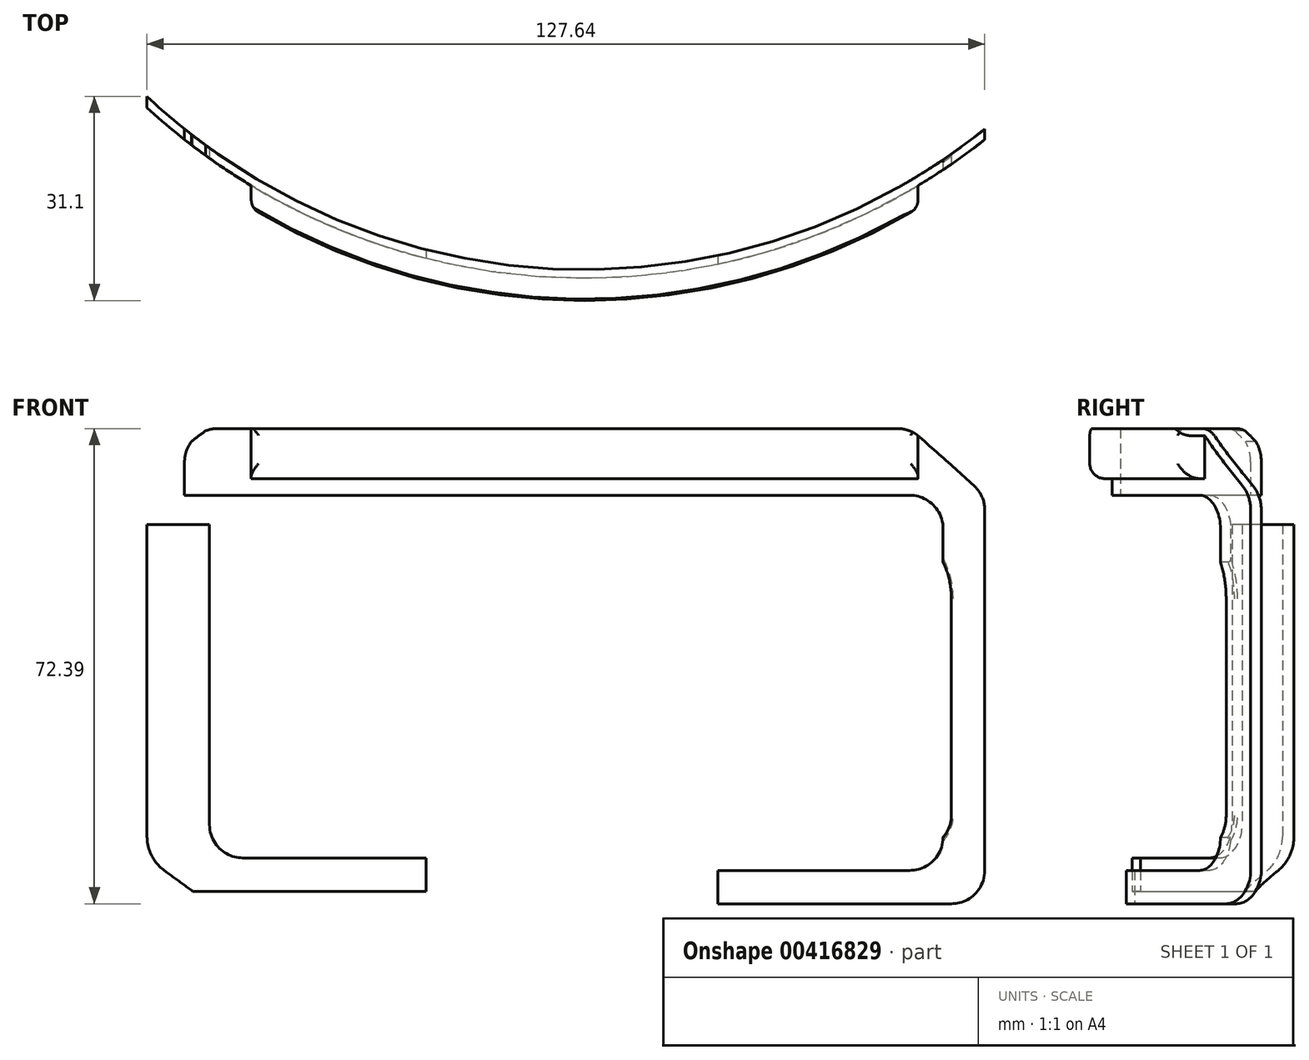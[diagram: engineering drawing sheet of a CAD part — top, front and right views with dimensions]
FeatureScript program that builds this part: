
annotation { "Feature Type Name" : "Feature", "Feature Type Description" : "" }
export const myFeature = defineFeature(function(context is Context, id is Id, definition is map)
    precondition{}
    {
        {
            var Q0;
            Q0=qCreatedBy(makeId("Top.planeOp"),FACE);
            var sketch = newSketch(context, id + "F0", { "sketchPlane" : qUnion([Q0])});
            skArc(sketch, "E0", {"start": v(-69.85, 28.98) * mm, "mid": v(0, 0) * mm, "end": v(69.85, 28.98) * mm});
            skLineSegment(sketch, "E1", {"start": v(0, 0) * mm, "end": v(0, 213.32) * mm, "construction": true});
            skArc(sketch, "E2", {"start": v(-69.85, 30.79) * mm, "mid": v(0, 1.27) * mm, "end": v(69.85, 30.79) * mm});
            skLineSegment(sketch, "E3", {"start": v(-69.85, 30.79) * mm, "end": v(-69.85, 28.98) * mm});
            skLineSegment(sketch, "E4", {"start": v(69.85, 30.79) * mm, "end": v(69.85, 28.98) * mm});
            skLineSegment(sketch, "E5", {"start": v(69.85, 30.79) * mm, "end": v(-69.85, 30.79) * mm, "construction": true});
            skSolve(sketch);
        }
        {
            var Q0;
            Q0=qSketchRegion(id+"F0",true);
            extrude(context, id + "F1", {"entities" : qUnion([Q0]), "depth" : 84.58 * mm, "offsetDistance" : 25.4 * mm});
        }
        {
            var Q0;
            Q0=makeQuery(id+"F1.opExtrude","CAP_EDGE",EDGE,{"disambiguationData":[OSD([sQuery(id+"F0.wireOp",EDGE,"E3")])],"isStart":false});
            var Q1;
            Q1=makeQuery(id+"F1.opExtrude","CAP_EDGE",EDGE,{"disambiguationData":[OSD([sQuery(id+"F0.wireOp",EDGE,"E4")])],"isStart":false});
            var Q2;
            Q2=makeQuery(id+"F1.opExtrude","CAP_EDGE",EDGE,{"disambiguationData":[OSD([sQuery(id+"F0.wireOp",EDGE,"E4")])],"isStart":true});
            var Q3;
            Q3=makeQuery(id+"F1.opExtrude","CAP_EDGE",EDGE,{"disambiguationData":[OSD([sQuery(id+"F0.wireOp",EDGE,"E3")])],"isStart":true});
            fillet(context, id + "F2", {"entities" : qUnion([Q0, Q1, Q2, Q3]), "radius" : 27.94 * mm, "tangentPropagation" : true, "allowEdgeOverflow" : false});
        }
        {
            var Q0;
            Q0=qCreatedBy(makeId("Front.planeOp"),FACE);
            var sketch = newSketch(context, id + "F3", { "sketchPlane" : qUnion([Q0])});
            skLineSegment(sketch, "E6", {"start": v(12.7, 0) * mm, "end": v(-12.7, 0) * mm});
            skLineSegment(sketch, "E7", {"start": v(-12.2, 1.88) * mm, "end": v(-7.16, 20.7) * mm});
            skLineSegment(sketch, "E8", {"start": v(7.16, 20.7) * mm, "end": v(12.2, 1.88) * mm});
            skLineSegment(sketch, "E9", {"start": v(14.65, 0) * mm, "end": v(22.86, 0) * mm});
            skLineSegment(sketch, "E10", {"start": v(-14.65, 0) * mm, "end": v(-22.86, 0) * mm});
            skPoint(sketch, "E11.visualSharp", {"position": v(12.7, 0) * mm});
            skArc(sketch, "E11.filletArc", {"start": v(12.2, 1.88) * mm, "mid": v(13.1, 0.52) * mm, "end": v(14.65, 0) * mm});
            skPoint(sketch, "E12.visualSharp", {"position": v(-12.7, 0) * mm});
            skArc(sketch, "E12.filletArc", {"start": v(-14.65, 0) * mm, "mid": v(-13.1, 0.52) * mm, "end": v(-12.2, 1.88) * mm});
            skLineSegment(sketch, "E13", {"start": v(-14.65, 0) * mm, "end": v(-12.7, 0) * mm});
            skLineSegment(sketch, "E14", {"start": v(12.7, 0) * mm, "end": v(14.65, 0) * mm});
            skLineSegment(sketch, "E15", {"start": v(-1.02, 25.4) * mm, "end": v(1.02, 25.4) * mm});
            skPoint(sketch, "E16.visualSharp", {"position": v(-5.9, 25.4) * mm});
            skArc(sketch, "E16.filletArc", {"start": v(-1.02, 25.4) * mm, "mid": v(-4.89, 24.09) * mm, "end": v(-7.16, 20.7) * mm});
            skPoint(sketch, "E17.visualSharp", {"position": v(5.9, 25.4) * mm});
            skArc(sketch, "E17.filletArc", {"start": v(7.16, 20.7) * mm, "mid": v(4.89, 24.09) * mm, "end": v(1.02, 25.4) * mm});
            skSolve(sketch);
        }
        {
            var Q0;
            Q0=qSketchRegion(id+"F3",true);
            extrude(context, id + "F4", {"entities" : qUnion([Q0]), "operationType" : NewBodyOperationType.REMOVE, "endBound" : BoundingType.THROUGH_ALL, "oppositeDirection" : true, "depth" : 25.4 * mm, "offsetDistance" : 25.4 * mm});
        }
        {
            var Q0;
            Q0=qCreatedBy(makeId("Front.planeOp"),FACE);
            var sketch = newSketch(context, id + "F5", { "sketchPlane" : qUnion([Q0])});
            skLineSegment(sketch, "E18.bottom", {"start": v(-43.18, 66.8) * mm, "end": v(43.18, 66.8) * mm});
            skLineSegment(sketch, "E18.left", {"start": v(-55.88, 54.1) * mm, "end": v(-55.88, 21.08) * mm});
            skLineSegment(sketch, "E18.right", {"start": v(55.88, 54.1) * mm, "end": v(55.88, 21.08) * mm});
            skPoint(sketch, "E19.visualSharp", {"position": v(-55.88, 66.8) * mm});
            skArc(sketch, "E19.filletArc", {"start": v(-43.18, 66.8) * mm, "mid": v(-52.16, 63.08) * mm, "end": v(-55.88, 54.1) * mm});
            skPoint(sketch, "E20.visualSharp", {"position": v(-55.88, 16) * mm});
            skArc(sketch, "E20.filletArc", {"start": v(-55.88, 21.08) * mm, "mid": v(-54.4, 17.49) * mm, "end": v(-50.8, 16) * mm});
            skPoint(sketch, "E21.visualSharp", {"position": v(55.88, 16) * mm});
            skArc(sketch, "E21.filletArc", {"start": v(50.8, 16) * mm, "mid": v(54.4, 17.49) * mm, "end": v(55.88, 21.08) * mm});
            skPoint(sketch, "E22.visualSharp", {"position": v(55.88, 66.8) * mm});
            skArc(sketch, "E22.filletArc", {"start": v(55.88, 54.1) * mm, "mid": v(52.16, 63.08) * mm, "end": v(43.18, 66.8) * mm});
            skLineSegment(sketch, "E23", {"start": v(50.8, 16) * mm, "end": v(19.1, 16) * mm});
            skLineSegment(sketch, "E24", {"start": v(-19.1, 16) * mm, "end": v(-50.8, 16) * mm});
            skLineSegment(sketch, "E25", {"start": v(0, 0) * mm, "end": v(0, 107.87) * mm, "construction": true});
            skLineSegment(sketch, "E26", {"start": v(-16.71, 17.67) * mm, "end": v(-15.74, 20.35) * mm});
            skLineSegment(sketch, "E27", {"start": v(-3.8, 28.7) * mm, "end": v(3.8, 28.7) * mm});
            skLineSegment(sketch, "E28", {"start": v(15.74, 20.35) * mm, "end": v(16.71, 17.67) * mm});
            skPoint(sketch, "E29.visualSharp", {"position": v(-12.7, 28.7) * mm});
            skArc(sketch, "E29.filletArc", {"start": v(-3.8, 28.7) * mm, "mid": v(-11.1, 26.4) * mm, "end": v(-15.74, 20.35) * mm});
            skPoint(sketch, "E30.visualSharp", {"position": v(12.7, 28.7) * mm});
            skArc(sketch, "E30.filletArc", {"start": v(15.74, 20.35) * mm, "mid": v(11.1, 26.4) * mm, "end": v(3.8, 28.7) * mm});
            skPoint(sketch, "E31.visualSharp", {"position": v(-17.32, 16) * mm});
            skArc(sketch, "E31.filletArc", {"start": v(-19.1, 16) * mm, "mid": v(-17.64, 16.46) * mm, "end": v(-16.71, 17.67) * mm});
            skPoint(sketch, "E32.visualSharp", {"position": v(17.32, 16) * mm});
            skArc(sketch, "E32.filletArc", {"start": v(16.71, 17.67) * mm, "mid": v(17.64, 16.46) * mm, "end": v(19.1, 16) * mm});
            skSolve(sketch);
        }
        {
            var Q0;
            Q0=qSketchRegion(id+"F5",true);
            extrude(context, id + "F6", {"entities" : qUnion([Q0]), "operationType" : NewBodyOperationType.REMOVE, "oppositeDirection" : true, "depth" : 76.2 * mm});
        }
        {
            var Q0;
            Q0=makeQuery(id+"F6.boolean.opBoolean","INTERSECT",EDGE,{"derivedFrom":[makeQuery(id+"F1.opExtrude","SWEPT_FACE",FACE,{"disambiguationData":[OSD([sQuery(id+"F0.wireOp",EDGE,"E0")])]}),makeQuery(id+"F6.opExtrude","SWEPT_FACE",FACE,{"disambiguationData":[OSD([sQuery(id+"F5.wireOp",EDGE,"E18.top")])]})]});
            var Q1;
            {var subQ0=sQuery(id+"F0.wireOp",EDGE,"E4");var subQ1=sQuery(id+"F0.wireOp",EDGE,"E2");Q1=makeQuery(id+"F6.boolean.opBoolean","INTERSECT",EDGE,{"derivedFrom":[makeQuery(id+"F2.opFillet","BLEND_FACE",FACE,{"disambiguationData":[OSD([subQ1,subQ0]),TDD([makeQuery(id+"F1.opExtrude","SWEPT_EDGE",EDGE,{"disambiguationData":[OSD([subQ1,subQ0])]})])]}),makeQuery(id+"F6.opExtrude","SWEPT_FACE",FACE,{"disambiguationData":[OSD([sQuery(id+"F5.wireOp",EDGE,"E18.right")])]})]});}
            var Q2;
            Q2=makeQuery(id+"F6.boolean.opBoolean","INTERSECT",EDGE,{"derivedFrom":[makeQuery(id+"F1.opExtrude","SWEPT_FACE",FACE,{"disambiguationData":[OSD([sQuery(id+"F0.wireOp",EDGE,"E2")])]}),makeQuery(id+"F6.opExtrude","SWEPT_FACE",FACE,{"disambiguationData":[OSD([sQuery(id+"F5.wireOp",EDGE,"E18.bottom")])]})]});
            fillet(context, id + "F7", {"entities" : qUnion([Q0, Q1, Q2]), "radius" : 0.64 * mm, "tangentPropagation" : true, "allowEdgeOverflow" : false});
        }
        {
            var Q0;
            Q0=qCreatedBy(makeId("Top.planeOp"),FACE);
            cPlane(context, id + "F8", {"entities" : qUnion([Q0]), "cplaneType" : CPlaneType.OFFSET, "offset" : 76.2 * mm, "width" : 152.4 * mm, "height" : 152.4 * mm});
        }
        {
            var Q0;
            Q0=qCreatedBy(id+"F8.planeOp",FACE);
            var sketch = newSketch(context, id + "F9", { "sketchPlane" : qUnion([Q0])});
            skArc(sketch, "E33", {"start": v(-50.8, 10.65) * mm, "mid": v(0, -3.43) * mm, "end": v(50.8, 10.65) * mm});
            skArc(sketch, "E34", {"start": v(-50.8, 14.68) * mm, "mid": v(0, 0) * mm, "end": v(50.8, 14.68) * mm});
            skLineSegment(sketch, "E35", {"start": v(-50.8, 10.65) * mm, "end": v(-50.8, 14.68) * mm});
            skLineSegment(sketch, "E36", {"start": v(50.8, 10.65) * mm, "end": v(50.8, 14.68) * mm});
            skSolve(sketch);
        }
        {
            var Q0;
            Q0=qSketchRegion(id+"F9",true);
            extrude(context, id + "F10", {"entities" : qUnion([Q0]), "operationType" : NewBodyOperationType.ADD, "depth" : 5.08 * mm, "offsetDistance" : 25.4 * mm, "hasSecondDirection" : true, "secondDirectionOppositeDirection" : true, "secondDirectionDepth" : 3.8 * mm});
        }
        {
            var Q0;
            Q0=makeQuery(id+"F10.opExtrude","SWEPT_FACE",FACE,{"disambiguationData":[OSD([sQuery(id+"F9.wireOp",EDGE,"E33")])]});
            fillet(context, id + "F11", {"entities" : qUnion([Q0]), "radius" : 2.3 * mm, "tangentPropagation" : true, "allowEdgeOverflow" : false});
        }
        {
            var Q0;
            Q0=qCreatedBy(makeId("Front.planeOp"),FACE);
            var sketch = newSketch(context, id + "F12", { "sketchPlane" : qUnion([Q0])});
            skLineSegment(sketch, "E37.bottom", {"start": v(19.05, 0) * mm, "end": v(-19.05, 0) * mm});
            skLineSegment(sketch, "E37.top", {"start": v(19.05, 38.1) * mm, "end": v(-19.05, 38.1) * mm});
            skLineSegment(sketch, "E37.left", {"start": v(19.05, 0) * mm, "end": v(19.05, 38.1) * mm});
            skLineSegment(sketch, "E37.right", {"start": v(-19.05, 0) * mm, "end": v(-19.05, 38.1) * mm});
            skSolve(sketch);
        }
        {
            var Q0;
            Q0 = qSketchRegion(id + "F12", true);
            extrude(context, id + "F13", {"entities" : qUnion([Q0]), "operationType" : NewBodyOperationType.REMOVE, "oppositeDirection" : true, "depth" : 25.4 * mm, "offsetDistance" : 25.4 * mm});
        }
        {
            var Q0;
            Q0=qCreatedBy(makeId("Front.planeOp"),FACE);
            var sketch = newSketch(context, id + "F14", { "sketchPlane" : qUnion([Q0])});
            skLineSegment(sketch, "E38.bottom", {"start": v(101.6, 0) * mm, "end": v(-101.6, 0) * mm});
            skLineSegment(sketch, "E38.top", {"start": v(101.6, 101.6) * mm, "end": v(-101.6, 101.6) * mm});
            skLineSegment(sketch, "E38.left", {"start": v(101.6, 0) * mm, "end": v(101.6, 101.6) * mm});
            skLineSegment(sketch, "E38.right", {"start": v(-101.6, 0) * mm, "end": v(-101.6, 101.6) * mm});
            skLineSegment(sketch, "E39", {"start": v(-24.13, 14.6) * mm, "end": v(-24.13, 9.52) * mm});
            skLineSegment(sketch, "E40", {"start": v(-59.7, 9.52) * mm, "end": v(-24.13, 9.52) * mm});
            skLineSegment(sketch, "E41", {"start": v(-24.13, 14.6) * mm, "end": v(-52.07, 14.6) * mm});
            skLineSegment(sketch, "E42", {"start": v(-57.15, 19.68) * mm, "end": v(-57.15, 65.4) * mm});
            skLineSegment(sketch, "E43", {"start": v(-57.15, 65.4) * mm, "end": v(-66.68, 65.4) * mm});
            skLineSegment(sketch, "E44", {"start": v(-66.68, 65.4) * mm, "end": v(-66.68, 17.84) * mm});
            skLineSegment(sketch, "E45", {"start": v(-64.06, 12.7) * mm, "end": v(-59.7, 9.52) * mm});
            skPoint(sketch, "E46.visualSharp", {"position": v(-66.67, 14.6) * mm});
            skArc(sketch, "E46.filletArc", {"start": v(-66.67, 17.84) * mm, "mid": v(-65.98, 14.96) * mm, "end": v(-64.06, 12.7) * mm});
            skPoint(sketch, "E47.visualSharp", {"position": v(-57.15, 14.6) * mm});
            skArc(sketch, "E47.filletArc", {"start": v(-57.15, 19.68) * mm, "mid": v(-55.66, 16.1) * mm, "end": v(-52.07, 14.6) * mm});
            skLineSegment(sketch, "E48", {"start": v(47.66, 80) * mm, "end": v(-55.88, 80) * mm});
            skLineSegment(sketch, "E49", {"start": v(49.53, 69.85) * mm, "end": v(-60.96, 69.85) * mm});
            skLineSegment(sketch, "E50", {"start": v(-60.96, 69.85) * mm, "end": v(-60.96, 74.93) * mm});
            skLineSegment(sketch, "E51", {"start": v(60.96, 67.58) * mm, "end": v(60.96, 12.7) * mm});
            skLineSegment(sketch, "E52", {"start": v(55.88, 7.62) * mm, "end": v(20.32, 7.62) * mm});
            skLineSegment(sketch, "E53", {"start": v(20.32, 7.62) * mm, "end": v(20.32, 12.7) * mm});
            skPoint(sketch, "E54.visualSharp", {"position": v(60.96, 7.62) * mm});
            skArc(sketch, "E54.filletArc", {"start": v(55.88, 7.62) * mm, "mid": v(59.47, 9.1) * mm, "end": v(60.96, 12.7) * mm});
            skPoint(sketch, "E55.visualSharp", {"position": v(-60.96, 80) * mm});
            skArc(sketch, "E55.filletArc", {"start": v(-55.88, 80) * mm, "mid": v(-59.47, 78.52) * mm, "end": v(-60.96, 74.93) * mm});
            skLineSegment(sketch, "E56", {"start": v(20.32, 12.7) * mm, "end": v(49.53, 12.7) * mm});
            skLineSegment(sketch, "E57", {"start": v(54.6, 17.78) * mm, "end": v(54.6, 64.77) * mm});
            skLineSegment(sketch, "E58", {"start": v(59.27, 71.36) * mm, "end": v(51.05, 78.72) * mm});
            skPoint(sketch, "E59.visualSharp", {"position": v(60.96, 69.85) * mm});
            skArc(sketch, "E59.filletArc", {"start": v(60.96, 67.58) * mm, "mid": v(60.52, 69.65) * mm, "end": v(59.27, 71.36) * mm});
            skPoint(sketch, "E60.visualSharp", {"position": v(49.6, 80.01) * mm});
            skArc(sketch, "E60.filletArc", {"start": v(51.05, 78.72) * mm, "mid": v(49.47, 79.68) * mm, "end": v(47.66, 80) * mm});
            skPoint(sketch, "E61.visualSharp", {"position": v(54.6, 69.85) * mm});
            skArc(sketch, "E61.filletArc", {"start": v(54.6, 64.77) * mm, "mid": v(53.12, 68.36) * mm, "end": v(49.53, 69.85) * mm});
            skPoint(sketch, "E62.visualSharp", {"position": v(54.6, 12.7) * mm});
            skArc(sketch, "E62.filletArc", {"start": v(49.53, 12.7) * mm, "mid": v(53.12, 14.19) * mm, "end": v(54.6, 17.78) * mm});
            skSolve(sketch);
        }
        {
            var Q0;
            Q0=makeQuery(id+"F14.imprint","IMPRINT",FACE,{"disambiguationData":[TD([[makeQuery(id+"F14.imprint","IMPRINT",EDGE,{"derivedFrom":sQuery(id+"F14.wireOp",EDGE,"E38.bottom")}),-1.0]])]});
            extrude(context, id + "F15", {"entities" : qUnion([Q0]), "operationType" : NewBodyOperationType.REMOVE, "endBound" : BoundingType.SYMMETRIC, "oppositeDirection" : true, "depth" : 127 * mm, "offsetDistance" : 25.4 * mm});
        }
    });
